# Revit family: PAV PS CIRC
name_source: partatom
category: Equipement de génie climatique
revit_build: Autodesk Revit 2018 (Build: 20170223_1515(x64)
units: mm (PartAtom-declared; Revit-internal decimal feet)

## family parameters
Basée sur le plan de construction = Non
Classification = Aucun
Cote de connecteur circulaire = Utiliser le diamètre
Couper avec des vides une fois chargée = Non
Partagée = Non
Point de calcul de pièce = Non
Toujours verticalement = Oui
Type d'élément = Normal

## types (4) — shared parameters
BRANCHEMENT_TERRE = Oui
COS_PHI = 0.9
DESCR_ALIM_X = Alimentation électrique, 3G1mm²
DIAMETRE.MOTEUR = 67 mm
DOUBLE_ALIMENTATION = Oui
HAUT.MOTEUR = 70 mm  [stored 0.229659 ft]
LARG.MOTEUR = 67 mm
NBR_POLES = 1
NEUTRE = Oui
NIVEAU_SONORE(dB(A)) = 57
POIDS(Kg) = 36 mm  [stored 0.11811 ft]
PUISS_APPARENTE_2 = 0 VA
PUISS_ELECT_2 = 0 kW
TENSION_ALIM = 230 V
Type_coffret = tableau éléctrique EPT : Coffret_PM2_3xSL150R
Zone de maintenance 1 = Oui
Zone de maintenance coffret = Oui
zero-valued in all types: HAUTEUR

## per-type parameters (varying)
| type | DEBIT_ASPI_VIDE | DEBIT_REFOUL_VIDE | DESCR_ASPI | DESCR_REFOUL | DIAM_ASPI_VIDE | DIAM_REFOUL_VIDE | HAUT.CONDO | HAUT.FLASQUE | LARG.ENTRAXE.GOUSSET | LARG.SOCLE | LONG.ENTRAXE.GOUSSET | LONG.FLASQUE | LONG.FLASQUE.TROU.VIDE | LONG.FLASQUE.VIDE | LONG.MOTEUR | LONG.SOCLE | PUISS_APPARENTE | PUISS_ELECT |
| 2V | 2.8 m³/h | 2.8 m³/h | Aspiration Vide; 2.8m3/h; G1/4"FEM | Refoulement Vide; 2.8m3/h; G1/4"FEM | 8 mm  [stored 0.0262467 ft] | 8 mm  [stored 0.0262467 ft] | 132 mm  [stored 0.433071 ft] | 198 mm  [stored 0.649606 ft] | 56 mm  [stored 0.183727 ft] | 65 mm  [stored 0.213255 ft] | 140.5 mm | 90.5 mm  [stored 0.296916 ft] | 240 mm  [stored 0.787402 ft] | 90.5 mm  [stored 0.296916 ft] | 181 mm  [stored 0.593832 ft] | 181 mm  [stored 0.593832 ft] | 278 VA | 0 kW |
| 5V | 4.8 m³/h | 4.8 m³/h | Aspiration Vide; 4.8m3/h; G1/4"FEM | Refoulement Vide; 4.8m3/h; G1/4"FEM | 8 mm  [stored 0.0262467 ft] | 8 mm  [stored 0.0262467 ft] | 132 mm  [stored 0.433071 ft] | 198 mm  [stored 0.649606 ft] | 56 mm  [stored 0.183727 ft] | 65 mm  [stored 0.213255 ft] | 196.5 mm | 240 mm  [stored 0.787402 ft] | 240 mm  [stored 0.787402 ft] | 59 mm | 240 mm  [stored 0.787402 ft] | 240 mm  [stored 0.787402 ft] | 333 VA | 0 kW |
| 7V | 6.4 m³/h | 6.4 m³/h | Aspiration Vide; 6.4m3/h; G1/4"FEM | Refoulement Vide; 6.4m3/h; G1/4"FEM | 8 mm  [stored 0.0262467 ft] | 8 mm  [stored 0.0262467 ft] | 132 mm  [stored 0.433071 ft] | 198 mm  [stored 0.649606 ft] | 56 mm  [stored 0.183727 ft] | 65 mm  [stored 0.213255 ft] | 196.5 mm | 240 mm  [stored 0.787402 ft] | 240 mm  [stored 0.787402 ft] | 59 mm | 240 mm  [stored 0.787402 ft] | 240 mm  [stored 0.787402 ft] | 422 VA | 0 kW |
| 12V | 10.0 m³/h | 10.0 m³/h | Aspiration Vide; 10m3/h; G3/8"FEM | Refoulement Vide; 10m3/h; G3/8"FEM | 10 mm  [stored 0.0328084 ft] | 10 mm  [stored 0.0328084 ft] | 142 mm  [stored 0.465879 ft] | 241.5 mm | 59 mm | 70 mm  [stored 0.229659 ft] | 234.5 mm | 275 mm | 275 mm | 94 mm  [stored 0.308399 ft] | 275 mm | 275 mm | 644 VA | 1 kW |

note: [stored X ft] marks values corroborated as IEEE doubles in the binary element streams (Revit-internal decimal feet)
